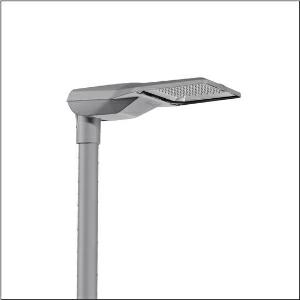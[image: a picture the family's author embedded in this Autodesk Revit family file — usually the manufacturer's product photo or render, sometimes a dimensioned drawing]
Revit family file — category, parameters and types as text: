
# Revit family: streetlight_sl_21_iq_midi___stw1_0a_5xe3e31d08mb_516a
name_source: partatom
category: Lighting Fixtures
units: mm (PartAtom-declared; Revit-internal decimal feet)

## family parameters
Cut with Voids When Loaded = No
Host = Face
Light Source = No
Part Type = Normal
Room Calculation Point = No
Round Connector Dimension = Use Diameter
Shared = No

## types (1)
- --- (1 x LED, 19500 lm, 146.7 W, 3000K)
    Apparent Load = 147 VA
    CIE Flux Codes = 38 75 98 100 100
    Color Rendering = 70
    Color Temperature = 3000K
    Default Elevation = 1800 mm
    Description = Streetlight SL 21 iQ midi, mast luminaire, primary light control with lens, of PMMA, primary optical cover: cover, of toughened safety glass, transparent, light distribution: STW1.0a, light emission: direct distribution, primary light characteristic: asymmetric, installation type: post-top, side-entry, LED, High Power LED, rated luminous flux: 19.500lm, luminous efficacy: 133lm/W, light colour: 730, colour temperature: 3000K, control: Auto-Match, Temp-Guard, Lumen-Switch, Night-Set, Smart-Wire, Light-Fading, Desk-Remote (wireless, voltage-free reading and setting of iQ features in the workshop via application-optimized NFC function/RFID function), optimised constant luminous flux control (CLO 2.0), presetting dimming linear, mains connection: 230..240V, AC, 50/60Hz, start of lifetime: 147W, end of service life: 161W, reduction: 62W, luminaire housing, of diecast aluminium, powder-coated, Siteco® metallic grey (DB 702S), corrosivity category C5 mid according to DIN EN ISO 12944, please order mast flange separately, inclination adjustable: 0°, 5°, 10°, 15°, sealing non-destructively replaceable, multi-level sealing system, length: 644mm, width: 335mm, height: 110mm, mast flange for spigot size: 42mm (side-entry): 5XC10008XM4, 60/48mm (side-entry/post-top): 5XC10108XM2, 76/60mm (side-entry/post-top): 5XC10108XM1, protection rating (complete): IP66, insulation class (complete): insulation class II (safety insulation), certification: CE, ENEC, ENEC+, VDE, impact resistance: IK09, permissible operating ambient temperature for outdoor applications: -40..+50°C, standard-compliant lighting for roads and squares, packaging unit: 1 piece

Light Distribution: STW1.0a
    Height = 111 mm
    Lamp = 1 x LED
    Lamp Light Flux = 19500 lm
    Lamp Power = 146.7 W
    Lamp count = 1
    Length = 644 mm
    Luminous efficacy = 133 lm/W
    Manufacturer = Siteco
    ModVariant = No
    Model = 5XE3E31D08MB
    Number of Poles = 1
    OnlyDefault = Yes
    Power Factor = 1
    Product Name = Streetlight SL 21 iQ midi | STW1.0a
    Product group = mast luminaire | pylon top
    ProductGroupID = 6100
    Protection Class = Protection class II
    Protection Degree = IP 66
    RLX_Detail_Level = 1
    RLX_Emergency_Light_Flux = 0 lm
    RLX_Emergency_Type = 0
    RLX_Emergency_Type_DB = No
    RlxData = <blob elided: 90621 chars, md5=f72e0d02>
    Socket = socket
    Standby Power = 0 W
    System Light Flux = 19499 lm
    System Power = 147 W
    Type Comments = factory setting: luminous flux: 100 % | dim-lin: 254 | 753 mA
    Type Image = l_1004298.jpg
    URL = http://relux.com
    VarID = @adj_140195
    Voltage = 0 V
    Weight = 0.00 kg
    Width = 336 mm

## geometry (parser evidence)
native form markers: Blend x4, Sweep x12
no freeform markers — native parametric forms only
